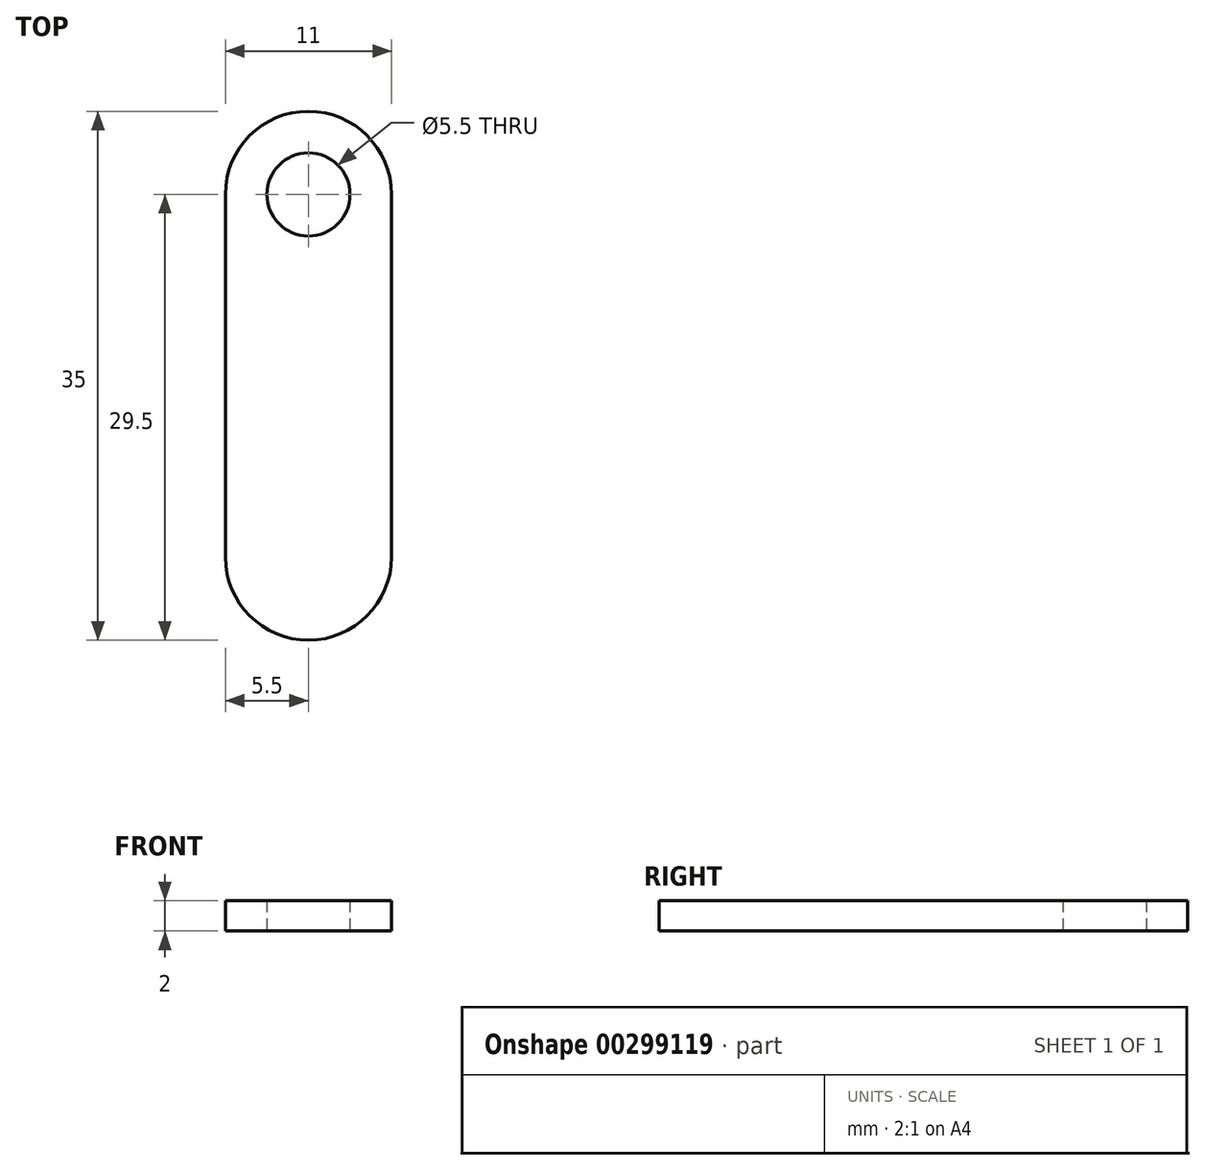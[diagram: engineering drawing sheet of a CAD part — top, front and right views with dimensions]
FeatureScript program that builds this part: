
annotation { "Feature Type Name" : "Feature", "Feature Type Description" : "" }
export const myFeature = defineFeature(function(context is Context, id is Id, definition is map)
    precondition{}
    {
        {
            var Q0;
            Q0=qCreatedBy(makeId("Top.planeOp"),FACE);
            var sketch = newSketch(context, id + "F0", { "sketchPlane" : qUnion([Q0])});
            skLineSegment(sketch, "E0", {"start": v(0, 24) * mm, "end": v(0, 0) * mm});
            skLineSegment(sketch, "E1", {"start": v(-11, 0) * mm, "end": v(-11, 24) * mm});
            skArc(sketch, "E2", {"start": v(0, 24) * mm, "mid": v(-5.5, 29.5) * mm, "end": v(-11, 24) * mm});
            skArc(sketch, "E3", {"start": v(-11, 0) * mm, "mid": v(-5.5, -5.5) * mm, "end": v(0, 0) * mm});
            skCircle(sketch, "E4", {"center": v(-5.5, 24) * mm, "radius": 2.75 * mm});
            skSolve(sketch);
        }
        {
            var Q0;
            Q0 = qSketchRegion(id + "F0", true);
            extrude(context, id + "F1", {"entities" : qUnion([Q0]), "depth" : 2 * mm});
        }
    });
